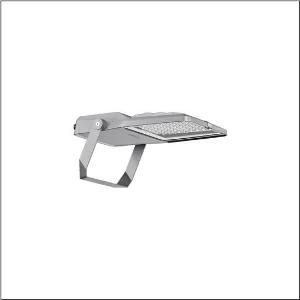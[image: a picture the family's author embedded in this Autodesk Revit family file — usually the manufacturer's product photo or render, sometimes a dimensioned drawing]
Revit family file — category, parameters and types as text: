
# Revit family: floodlight_fl_21_iq_mini___pl64_5xa7772b4e1a_46a5
name_source: partatom
category: Lighting Fixtures
units: mm (PartAtom-declared; Revit-internal decimal feet)

## family parameters
Cut with Voids When Loaded = No
Host = Face
Light Source = No
Part Type = Normal
Room Calculation Point = No
Round Connector Dimension = Use Diameter
Shared = No

## types (1)
- --- (1 x LED, 6270 lm, 45.5 W, 4000K)
    Apparent Load = 46 VA
    CIE Flux Codes = 28 80 98 100 100
    Color Rendering = 70
    Color Temperature = 4000K
    Default Elevation = 1800 mm
    Description = Floodlight FL 21 iQ mini, floodlight, primary light control with lens, of PMMA, primary optical cover: protective disc, of toughened safety glass, transparent, light distribution: PL64, light emission: direct distribution, installation type: surface-mounted, lamps: LED, High Power LED, rated values: 6.270lm | 45,5W | 137,8lm/W (begin service life); end service life: 6.270lm | 48W; at 50% lumin. flux: 3.135lm | 21,5W | 145,8lm/W, colour temperature: 4000K, colour rendering: CRI > 70, light colour: 740, light setting 1 begin service life: 100% | 6.270lm | 45,5W | 137,8lm/W | 4.000K, light setting 1 end service life: 48W, further light settings possible, control: Street-Remote, Auto-Match, Temp-Guard, Night-Set, Smart-Wire, Desk-Remote (wireless, voltage-free reading and setting of iQ features in the workshop via application-optimized NFC function/RFID function), optimised constant luminous flux control (CLO 2.0), pre-setting: linear dimming characteristic, with terminal, 6-pole, mains connection: 220..240V, AC, 50/60Hz, luminaire housing, of diecast aluminium, powder-coated, SITECO metallic grey (DB 702S), corrosivity category C5 mid according to DIN EN ISO 12944suitable for swimming poolschlorine-resistant, sealing non-destructively replaceable, mounting bracket, of steel, galvanised, powder-coated, SITECO metallic grey (DB 702S), protection rating (complete): IP66, insulation class (complete): insulation class II (safety insulation), certification: CE, ENEC, VDE, protection symbol: D, impact resistance: IK08, permissible operating ambient temperature: -40..+40°C, permissible operating ambient temperature for outdoor applications: -40..+50°C, standard: DIN EN 12944, LABS conformity tested according to VDMA 24364:2018-05, packaging unit: 1 piece

Light Distribution: PL64
    Height = 70 mm
    Lamp = 1 x LED
    Lamp Light Flux = 6270 lm
    Lamp Power = 45.5 W
    Lamp count = 1
    Length = 485 mm
    Luminous efficacy = 138 lm/W
    Manufacturer = Siteco
    ModVariant = No
    Model = 5XA7772B4E1A
    Mounting Place = Pole
    Mounting Type = Pole annexe
    Number of Poles = 1
    OnlyDefault = Yes
    Power Factor = 1
    Product Name = Floodlight FL 21 iQ mini | PL64
    Product group = floodlight | pylon annexe
    ProductGroupID = 6201
    Protection Class = Protection class II
    Protection Degree = IP 66
    RLX_Detail_Level = 1
    RLX_Emergency_Light_Flux = 0 lm
    RLX_Emergency_Type = 0
    RLX_Emergency_Type_DB = No
    RlxData = <blob elided: 96449 chars, md5=90e8f735>
    Socket = socket
    Standby Power = 0 W
    System Light Flux = 6270 lm
    System Power = 46 W
    Type Comments = factory setting: luminous flux: 100 % | dim-lin: 254 | 463 mA
    Type Image = l_1006845.jpg
    URL = http://relux.com
    VarID = @adj_167863
    Voltage = 0 V
    Weight = 0.00 kg
    Width = 337 mm

## geometry (parser evidence)
native form markers: Blend x4, Sweep x11
no freeform markers — native parametric forms only
